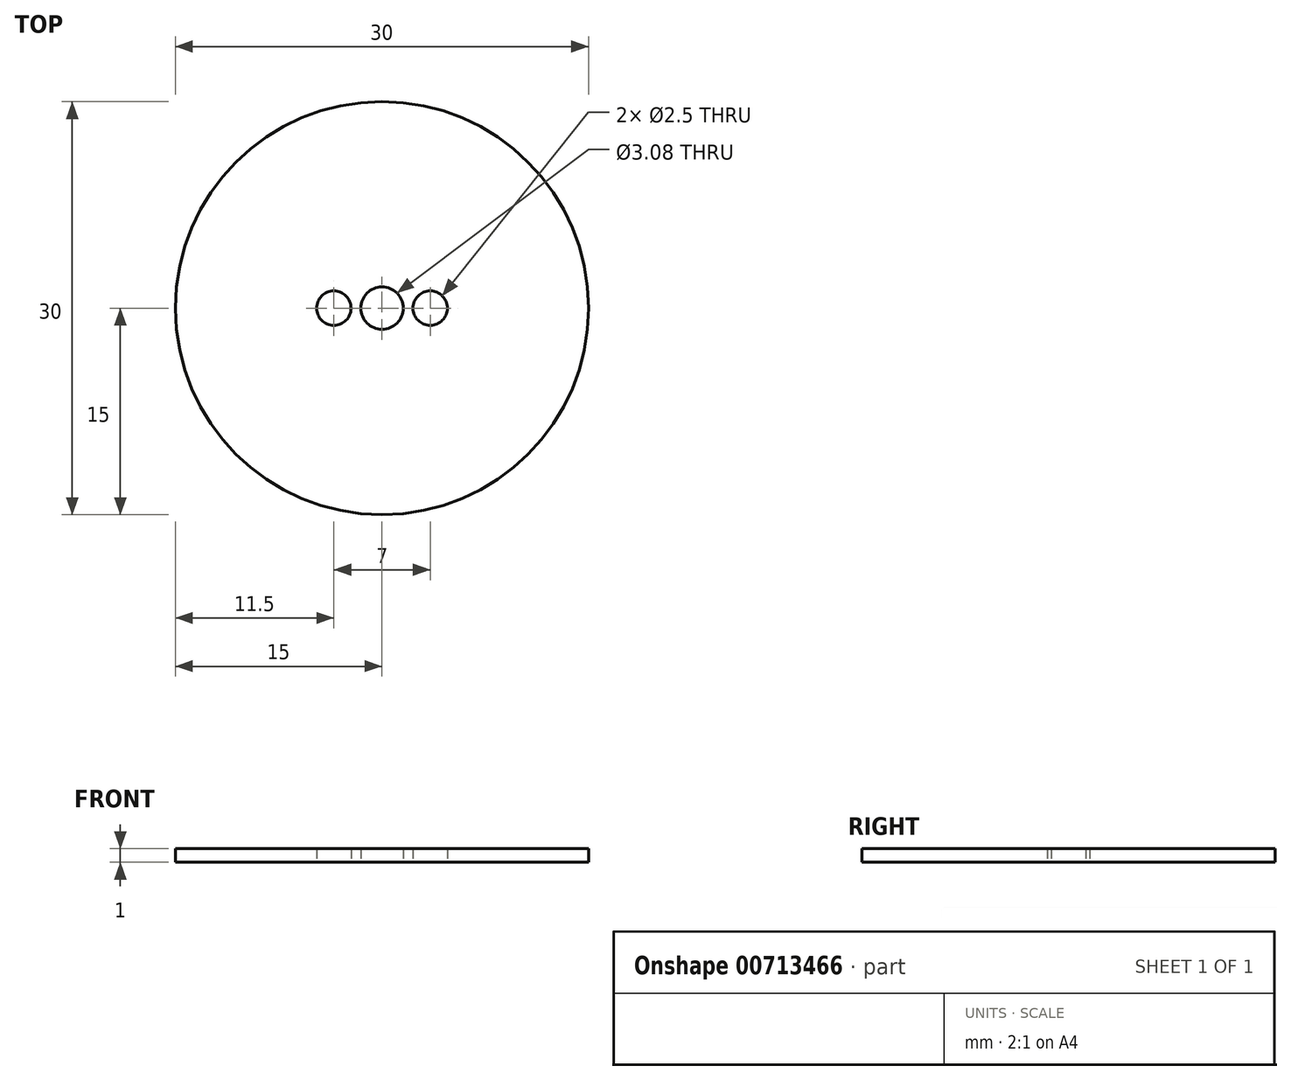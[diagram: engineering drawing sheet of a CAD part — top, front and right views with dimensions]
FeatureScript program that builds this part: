
annotation { "Feature Type Name" : "Feature", "Feature Type Description" : "" }
export const myFeature = defineFeature(function(context is Context, id is Id, definition is map)
    precondition{}
    {
        {
            var Q0;
            Q0=qCreatedBy(makeId("Top.planeOp"),FACE);
            var sketch = newSketch(context, id + "F0", { "sketchPlane" : qUnion([Q0])});
            skCircle(sketch, "E0", {"center": v(0, 0) * mm, "radius": 15 * mm});
            skCircle(sketch, "E1", {"center": v(0, 0) * mm, "radius": 1.54 * mm});
            skCircle(sketch, "E2", {"center": v(3.5, 0) * mm, "radius": 1.25 * mm});
            skLineSegment(sketch, "E3", {"start": v(0, 0) * mm, "end": v(0, 11.59) * mm, "construction": true});
            skCircle(sketch, "E4.MirrorC", {"center": v(-3.5, 0) * mm, "radius": 1.25 * mm});
            skSolve(sketch);
        }
        {
            var Q0;
            Q0 = qSketchRegion(id + "F0", true);
            extrude(context, id + "F1", {"entities" : qUnion([Q0]), "depth" : 1 * mm, "offsetDistance" : 25 * mm});
        }
    });
